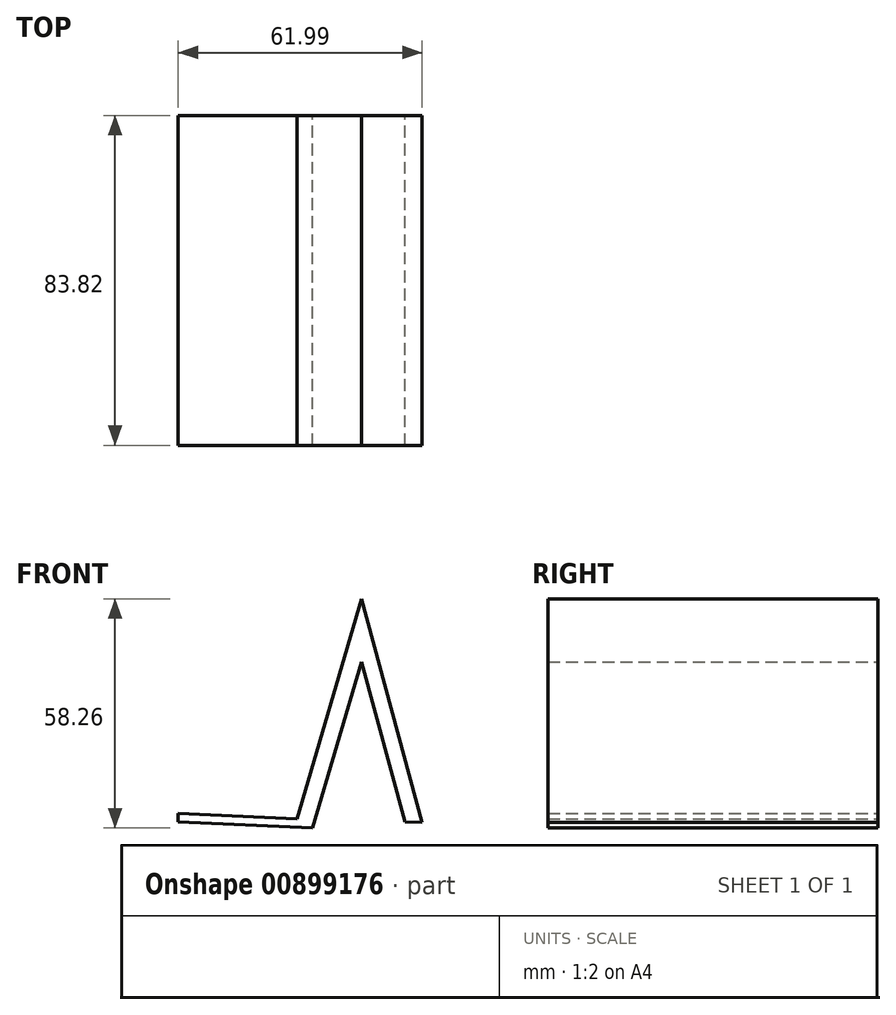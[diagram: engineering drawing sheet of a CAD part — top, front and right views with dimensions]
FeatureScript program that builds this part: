
annotation { "Feature Type Name" : "Feature", "Feature Type Description" : "" }
export const myFeature = defineFeature(function(context is Context, id is Id, definition is map)
    precondition{}
    {
        {
            var Q0;
            Q0=qCreatedBy(makeId("Front.planeOp"),FACE);
            var sketch = newSketch(context, id + "F0", { "sketchPlane" : qUnion([Q0])});
            skLineSegment(sketch, "E0", {"start": v(12.36, 38.3) * mm, "end": v(-4.53, -19.36) * mm});
            skLineSegment(sketch, "E1", {"start": v(12.36, 38.3) * mm, "end": v(27.8, -18.54) * mm});
            skLineSegment(sketch, "E2", {"start": v(12.36, 22.24) * mm, "end": v(23.4, -18.39) * mm});
            skLineSegment(sketch, "E3", {"start": v(12.36, 22.24) * mm, "end": v(0, -19.95) * mm});
            skLineSegment(sketch, "E4", {"start": v(23.4, -18.39) * mm, "end": v(27.8, -18.54) * mm});
            skLineSegment(sketch, "E5", {"start": v(0, -19.95) * mm, "end": v(-34.19, -18.39) * mm});
            skLineSegment(sketch, "E6", {"start": v(-4, -17.57) * mm, "end": v(-34.2, -16.2) * mm});
            skLineSegment(sketch, "E7", {"start": v(-34.2, -16.2) * mm, "end": v(-34.19, -18.39) * mm});
            skSolve(sketch);
        }
        {
            var Q0;
            {var subQ0=sQuery(id+"F0.wireOp",EDGE,"E1");Q0=makeQuery(id+"F0.imprint","IMPRINT",FACE,{"disambiguationData":[TD([[makeQuery(id+"F0.imprint","IMPRINT",EDGE,{"derivedFrom":subQ0}),-1.0]])]});}
            extrude(context, id + "F1", {"entities" : qUnion([Q0]), "depth" : 83.82 * mm, "offsetDistance" : 25.4 * mm});
        }
    });
